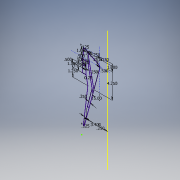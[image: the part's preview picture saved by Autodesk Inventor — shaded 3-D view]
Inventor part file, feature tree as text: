
AUTODESK INVENTOR PART (.ipt)
format: ipt  version: 2017 SP1 (Build 210196100, 196)  size: 129,024 bytes
history: native  units: in
note: dims shown in document units (in); Inventor stores cm internally (conversion verified against a paired STEP export)
features: sketch x1
ambient origin geometry x8: Origin, YZ Plane, XZ Plane, XY Plane, X Axis, Y Axis, Z Axis, Center Point
feature tree (1):
  sketch  "Sketch1"  dims[d0=1.13in d3=0.1718in d5=1.0in d6=1.0in d7=90.0deg d8=0.5in d9=15.0deg d31=0.25in d34=15.0deg d37=1.75in d40=3.75in d41=0.125in d46=0.75in d47=0.5in d51=0.5in d52=0.25in d54=0.5in d55=0.5in d56=1.25in d58=0.0017in d59=0.5in d60=0.5in d61=1.0in d62=0.234in d63=0.234in d64=0.125in d67=0.25in d68=4.25in d69=0.25in d70=0.25in d71=0.125in d73=3.4in d74=1.25in d75=0.2498in]
